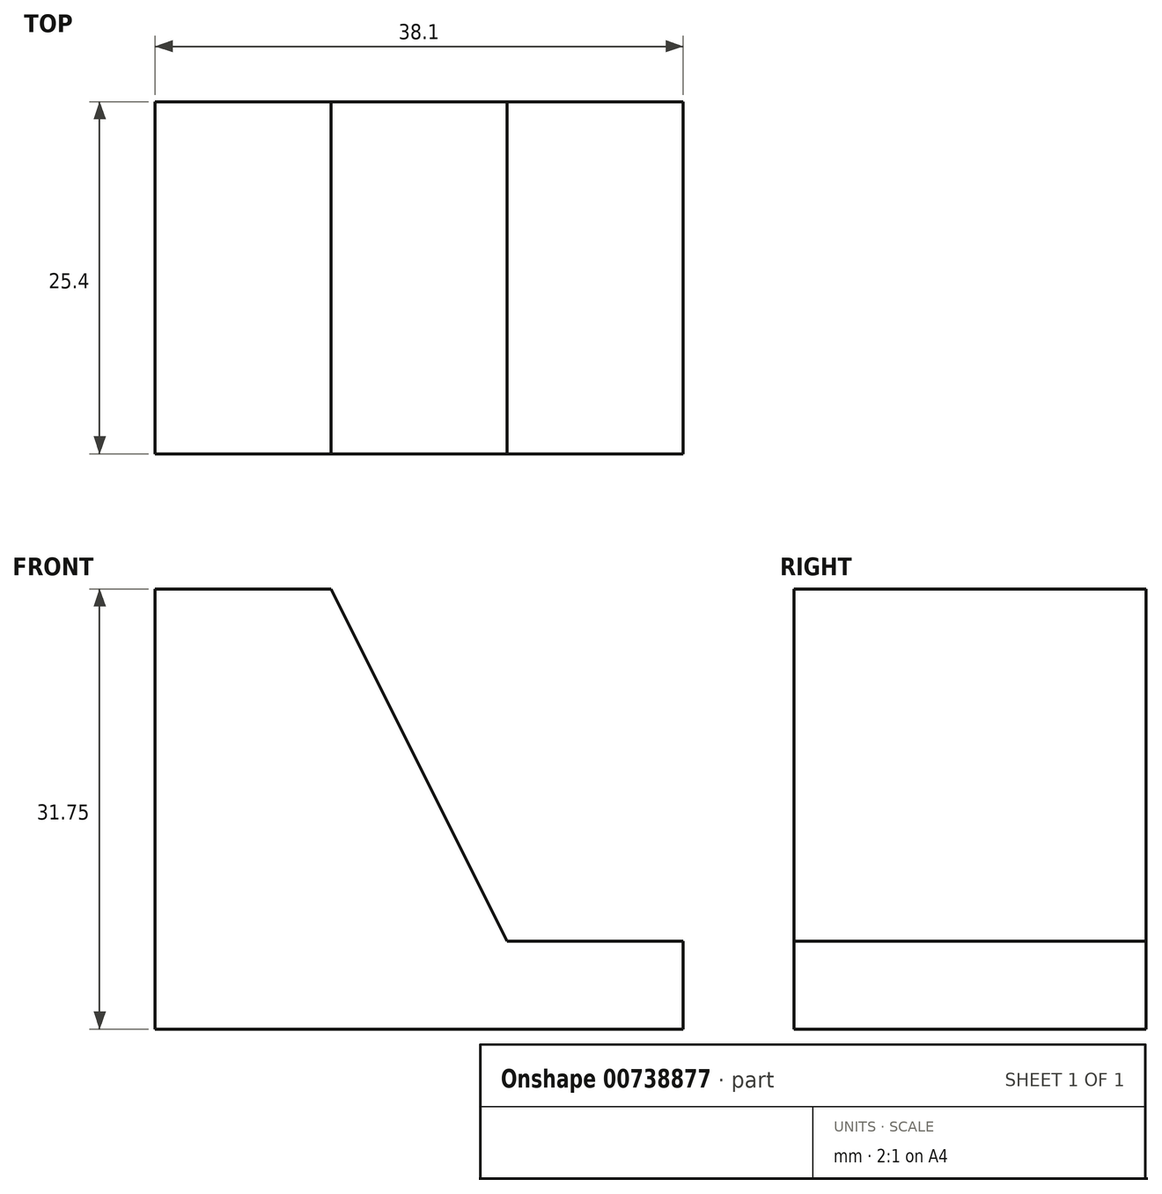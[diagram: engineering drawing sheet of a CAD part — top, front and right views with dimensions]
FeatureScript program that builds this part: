
annotation { "Feature Type Name" : "Feature", "Feature Type Description" : "" }
export const myFeature = defineFeature(function(context is Context, id is Id, definition is map)
    precondition{}
    {
        {
            var Q0;
            Q0=qCreatedBy(makeId("Front.planeOp"),FACE);
            var sketch = newSketch(context, id + "F0", { "sketchPlane" : qUnion([Q0])});
            skLineSegment(sketch, "E0", {"start": v(0, 31.75) * mm, "end": v(0, 0) * mm});
            skLineSegment(sketch, "E1", {"start": v(0, 0) * mm, "end": v(38.1, 0) * mm});
            skLineSegment(sketch, "E2", {"start": v(38.1, 0) * mm, "end": v(38.1, 31.75) * mm});
            skLineSegment(sketch, "E3", {"start": v(38.1, 31.75) * mm, "end": v(0, 31.75) * mm});
            skSolve(sketch);
        }
        {
            var Q0;
            Q0=makeQuery(id+"F0.imprint","IMPRINT",FACE,{"disambiguationData":[TD([[makeQuery(id+"F0.imprint","IMPRINT",EDGE,{"derivedFrom":sQuery(id+"F0.wireOp",EDGE,"E0")}),1.0]])]});
            extrude(context, id + "F1", {"entities" : qUnion([Q0]), "depth" : 25.4 * mm, "offsetDistance" : 25.4 * mm});
        }
        {
            var Q0;
            Q0=makeQuery(id+"F1.opExtrude","CAP_FACE",FACE,{"disambiguationData":[OSD([sQuery(id+"F0.wireOp",EDGE,"E0"),sQuery(id+"F0.wireOp",EDGE,"E1"),sQuery(id+"F0.wireOp",EDGE,"E2"),sQuery(id+"F0.wireOp",EDGE,"E3")])],"isStart":false});
            var sketch = newSketch(context, id + "F2", { "sketchPlane" : qUnion([Q0])});
            skLineSegment(sketch, "E4", {"start": v(25.4, 31.75) * mm, "end": v(25.4, 6.35) * mm});
            skLineSegment(sketch, "E5", {"start": v(25.4, 6.35) * mm, "end": v(38.1, 6.35) * mm});
            skLineSegment(sketch, "E6", {"start": v(12.7, 31.75) * mm, "end": v(25.4, 6.35) * mm});
            skSolve(sketch);
        }
        {
            var Q0;
            Q0 = qSketchRegion(id + "F2", true);
            var Q1;
            {var subQ0=sQuery(id+"F2.wireOp",EDGE,"E4");Q1=makeQuery(id+"F2.imprint","IMPRINT",FACE,{"disambiguationData":[TD([[makeQuery(id+"F2.imprint","IMPRINT",EDGE,{"derivedFrom":subQ0}),-1.0]])]});}
            var Q2;
            {var subQ0=sQuery(id+"F2.wireOp",EDGE,"E4");Q2=makeQuery(id+"F2.imprint","IMPRINT",FACE,{"disambiguationData":[TD([[makeQuery(id+"F2.imprint","IMPRINT",EDGE,{"derivedFrom":subQ0}),1.0]])]});}
            extrude(context, id + "F3", {"entities" : qUnion([Q0, Q1, Q2]), "operationType" : NewBodyOperationType.REMOVE, "endBound" : BoundingType.THROUGH_ALL, "oppositeDirection" : true, "depth" : 25.4 * mm, "offsetDistance" : 25.4 * mm});
        }
    });
